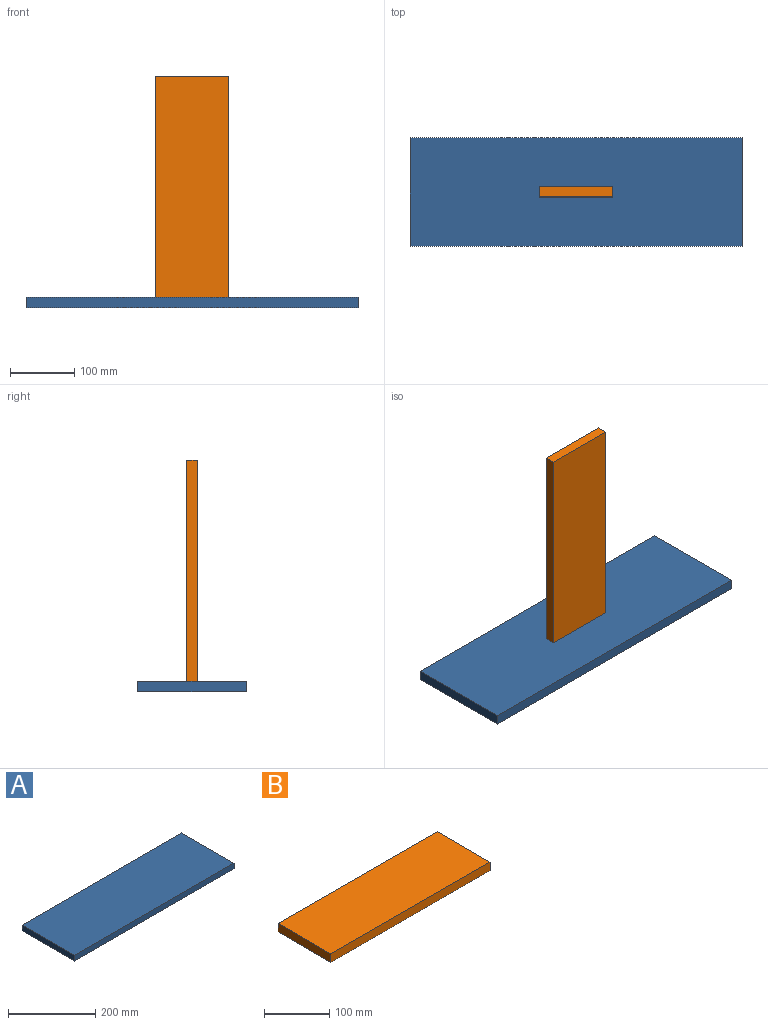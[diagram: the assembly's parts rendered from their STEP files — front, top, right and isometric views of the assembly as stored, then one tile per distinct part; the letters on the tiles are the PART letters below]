
ASSEMBLY  parts=2 mates=1
PART A: 6 faces, bbox 518x170x16 mm
  f0: plane 518x16mm, normal (0,1,0), area 8288mm2, adj f1,f3,f4,f5
  f1: plane 170x16mm, normal (-1,0,0), area 2720mm2, adj f0,f2,f4,f5
  f2: plane 518x16mm, normal (0,-1,0), area 8288mm2, adj f1,f3,f4,f5
  f3: plane 170x16mm, normal (1,0,0), area 2720mm2, adj f0,f2,f4,f5
  f4: plane 518x170mm, normal (0,0,1), area 88060mm2, adj f0,f1,f2,f3
  f5: plane 518x170mm, normal (0,0,-1), area 88060mm2, adj f0,f1,f2,f3
PART B: 6 faces, bbox 345.2x115.1x16 mm
  f0: plane 345.18x16mm, normal (0,-1,0), area 5522.8mm2, adj f1,f3,f4,f5
  f1: plane 115.06x16mm, normal (1,0,0), area 1840.9mm2, adj f0,f2,f4,f5
  f2: plane 345.18x16mm, normal (0,1,0), area 5522.8mm2, adj f1,f3,f4,f5
  f3: plane 115.06x16mm, normal (-1,0,0), area 1840.9mm2, adj f0,f2,f4,f5
  f4: plane 345.18x115.06mm, normal (0,0,1), area 39715.9mm2, adj f0,f1,f2,f3
  f5: plane 345.18x115.06mm, normal (0,0,-1), area 39715.9mm2, adj f0,f1,f2,f3
PLACE A t=(579.01,-32.62,76.82)mm fixed
PLACE B rot(axis=(-0.58,-0.58,-0.58),120deg) t=(296.87,358.11,727.17)mm
MATE planar B.f3 <-> A.f4  axis (0,0,-1) through (453.74,366.11,92.82)mm
